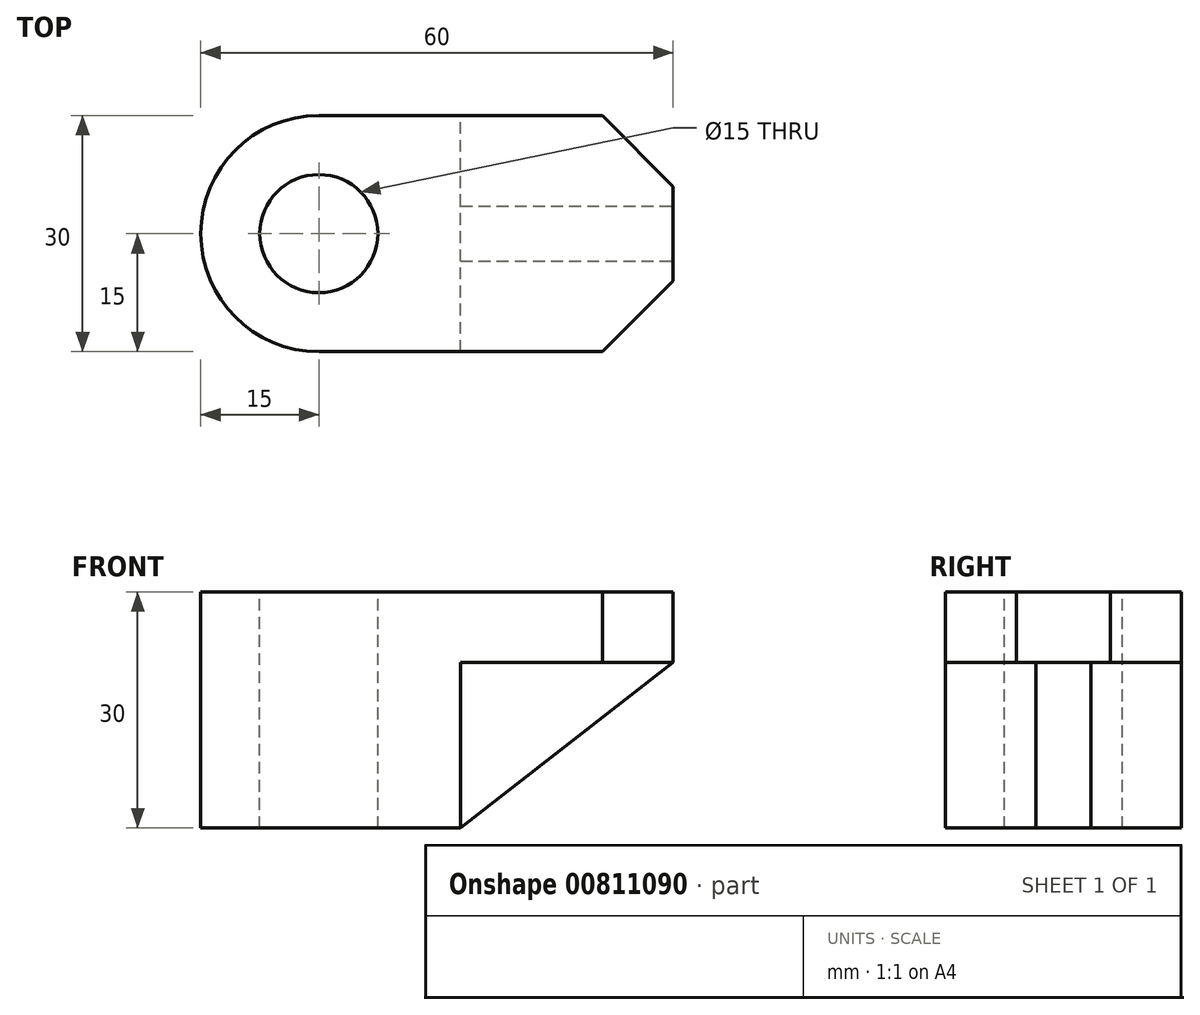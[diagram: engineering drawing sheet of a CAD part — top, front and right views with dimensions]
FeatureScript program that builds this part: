
annotation { "Feature Type Name" : "Feature", "Feature Type Description" : "" }
export const myFeature = defineFeature(function(context is Context, id is Id, definition is map)
    precondition{}
    {
        {
            var Q0;
            Q0=qCreatedBy(makeId("Top.planeOp"),FACE);
            var sketch = newSketch(context, id + "F0", { "sketchPlane" : qUnion([Q0])});
            skPoint(sketch, "E0.middle", {"position": v(0, 0) * mm});
            skLineSegment(sketch, "E1", {"start": v(-15, 15) * mm, "end": v(21, 15) * mm});
            skLineSegment(sketch, "E2", {"start": v(-15, -15) * mm, "end": v(21, -15) * mm});
            skLineSegment(sketch, "E3", {"start": v(30, 6) * mm, "end": v(30, -6) * mm});
            skLineSegment(sketch, "E4", {"start": v(21, 15) * mm, "end": v(30, 6) * mm});
            skLineSegment(sketch, "E5", {"start": v(30, -6) * mm, "end": v(21, -15) * mm});
            skArc(sketch, "E6", {"start": v(-15, 15) * mm, "mid": v(-30, 0) * mm, "end": v(-15, -15) * mm});
            skSolve(sketch);
        }
        {
            var Q0;
            Q0 = qSketchRegion(id + "F0", true);
            extrude(context, id + "F1", {"entities" : qUnion([Q0]), "depth" : 30 * mm, "offsetDistance" : 25 * mm});
        }
        {
            var Q0;
            Q0=makeQuery(id+"F1.opExtrude","CAP_FACE",FACE,{"disambiguationData":[OSD([sQuery(id+"F0.wireOp",EDGE,"E1"),sQuery(id+"F0.wireOp",EDGE,"E2"),sQuery(id+"F0.wireOp",EDGE,"E3"),sQuery(id+"F0.wireOp",EDGE,"E4"),sQuery(id+"F0.wireOp",EDGE,"E5"),sQuery(id+"F0.wireOp",EDGE,"E6")])],"isStart":false});
            var sketch = newSketch(context, id + "F2", { "sketchPlane" : qUnion([Q0])});
            skCircle(sketch, "E7", {"center": v(-15, 0) * mm, "radius": 7.5 * mm});
            skSolve(sketch);
        }
        {
            var Q0;
            Q0 = qSketchRegion(id + "F2", true);
            extrude(context, id + "F3", {"entities" : qUnion([Q0]), "operationType" : NewBodyOperationType.REMOVE, "oppositeDirection" : true, "depth" : 30 * mm, "offsetDistance" : 25 * mm});
        }
        {
            var Q0;
            Q0=makeQuery(id+"F1.opExtrude","CAP_FACE",FACE,{"disambiguationData":[OSD([sQuery(id+"F0.wireOp",EDGE,"E1"),sQuery(id+"F0.wireOp",EDGE,"E2"),sQuery(id+"F0.wireOp",EDGE,"E3"),sQuery(id+"F0.wireOp",EDGE,"E4"),sQuery(id+"F0.wireOp",EDGE,"E5"),sQuery(id+"F0.wireOp",EDGE,"E6")])],"isStart":true});
            var sketch = newSketch(context, id + "F4", { "sketchPlane" : qUnion([Q0])});
            skPoint(sketch, "E8.0", {"position": v(-15, 15) * mm});
            skLineSegment(sketch, "E9", {"start": v(-15, 15) * mm, "end": v(3, 15) * mm, "construction": true});
            skLineSegment(sketch, "E10", {"start": v(3, 15) * mm, "end": v(3, -15) * mm});
            skLineSegment(sketch, "E11", {"start": v(3, -15) * mm, "end": v(21, -15) * mm});
            skLineSegment(sketch, "E12", {"start": v(21, -15) * mm, "end": v(30, -6) * mm});
            skLineSegment(sketch, "E13", {"start": v(30, -6) * mm, "end": v(30, 6) * mm});
            skLineSegment(sketch, "E14", {"start": v(30, 6) * mm, "end": v(21, 15) * mm});
            skLineSegment(sketch, "E15", {"start": v(21, 15) * mm, "end": v(3, 15) * mm});
            skSolve(sketch);
        }
        {
            var Q0;
            Q0 = qSketchRegion(id + "F4", true);
            extrude(context, id + "F5", {"entities" : qUnion([Q0]), "operationType" : NewBodyOperationType.REMOVE, "oppositeDirection" : true, "depth" : 21 * mm, "offsetDistance" : 25 * mm});
        }
        {
            var Q0;
            Q0=makeQuery(id+"F5.boolean.opBoolean","COPY",FACE,{"derivedFrom":makeQuery(id+"F5.opExtrude","CAP_FACE",FACE,{"disambiguationData":[OSD([sQuery(id+"F4.wireOp",EDGE,"E10"),sQuery(id+"F4.wireOp",EDGE,"E11"),sQuery(id+"F4.wireOp",EDGE,"E12"),sQuery(id+"F4.wireOp",EDGE,"E13"),sQuery(id+"F4.wireOp",EDGE,"E14"),sQuery(id+"F4.wireOp",EDGE,"E15")])],"isStart":false})});
            var sketch = newSketch(context, id + "F6", { "sketchPlane" : qUnion([Q0])});
            skLineSegment(sketch, "E16.0", {"start": v(3, 15) * mm, "end": v(3, -15) * mm, "construction": true});
            skLineSegment(sketch, "E17", {"start": v(3, 3.5) * mm, "end": v(30, 3.5) * mm});
            skLineSegment(sketch, "E18.MirrorCS", {"start": v(3, -3.5) * mm, "end": v(30, -3.5) * mm});
            skLineSegment(sketch, "E19", {"start": v(30, 3.5) * mm, "end": v(30, -3.5) * mm});
            skLineSegment(sketch, "E20", {"start": v(3, 3.5) * mm, "end": v(3, -3.5) * mm});
            skSolve(sketch);
        }
        {
            var Q0;
            Q0 = qSketchRegion(id + "F6", true);
            extrude(context, id + "F7", {"entities" : qUnion([Q0]), "operationType" : NewBodyOperationType.ADD, "depth" : 21 * mm, "offsetDistance" : 25 * mm});
        }
        {
            var Q0;
            Q0=makeQuery(id+"F7.opExtrude","SWEPT_FACE",FACE,{"disambiguationData":[OSD([sQuery(id+"F6.wireOp",EDGE,"E18.MirrorCS")])]});
            var sketch = newSketch(context, id + "F8", { "sketchPlane" : qUnion([Q0])});
            skLineSegment(sketch, "E21", {"start": v(-3, 0) * mm, "end": v(-30, 21) * mm});
            skLineSegment(sketch, "E22", {"start": v(-30, 21) * mm, "end": v(-30, 0) * mm});
            skLineSegment(sketch, "E23", {"start": v(-30, 0) * mm, "end": v(-3, 0) * mm});
            skSolve(sketch);
        }
        {
            var Q0;
            Q0 = qSketchRegion(id + "F8", true);
            extrude(context, id + "F9", {"entities" : qUnion([Q0]), "operationType" : NewBodyOperationType.REMOVE, "oppositeDirection" : true, "depth" : 25 * mm, "offsetDistance" : 25 * mm});
        }
    });
